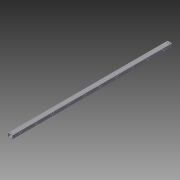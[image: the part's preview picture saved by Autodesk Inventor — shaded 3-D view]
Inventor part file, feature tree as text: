
AUTODESK INVENTOR PART (.ipt)
format: ipt  version: 2015 SP1 (Build 190203100, 203)  size: 179,712 bytes
history: native  units: in
note: dims shown in document units (in); Inventor stores cm internally (conversion verified against a paired STEP export)
features: extrude x3, sketch x2
ambient origin geometry x8: Origin, YZ Plane, XZ Plane, XY Plane, X Axis, Y Axis, Z Axis, Center Point
bodies: Solid1 (feature_tree)
feature tree (5):
  extrude  "Extrusion1"  Depth=1.1811in
  extrude  "Extrusion2"  Depth=56.2992in TaperAngle=0.0deg
  extrude  "Extrusion3"  Depth=0.0787in
  sketch  "Sketch3"  dims[d0=1.5748in d1=1.1811in]
  sketch  "Sketch4"  dims[d3=0.0787in d4=56.2992in d5=0.0in d6=0.0787in d7=0.0787in d8=0.0787in d14=3.937in d16=5.6299in d17=0.3937in d19=0.3937in d21=0.3937in d22=0.0in d23=0.2756in d24=0.4921in d25=0.7087in d26=0.4921in d27=0.0in d28=0.0in d43=0.2756in d44=2.815in d45=0.7874in d46=0.4724in d47=3.937in d49=5.6299in d50=0.3937in d52=0.3937in]
